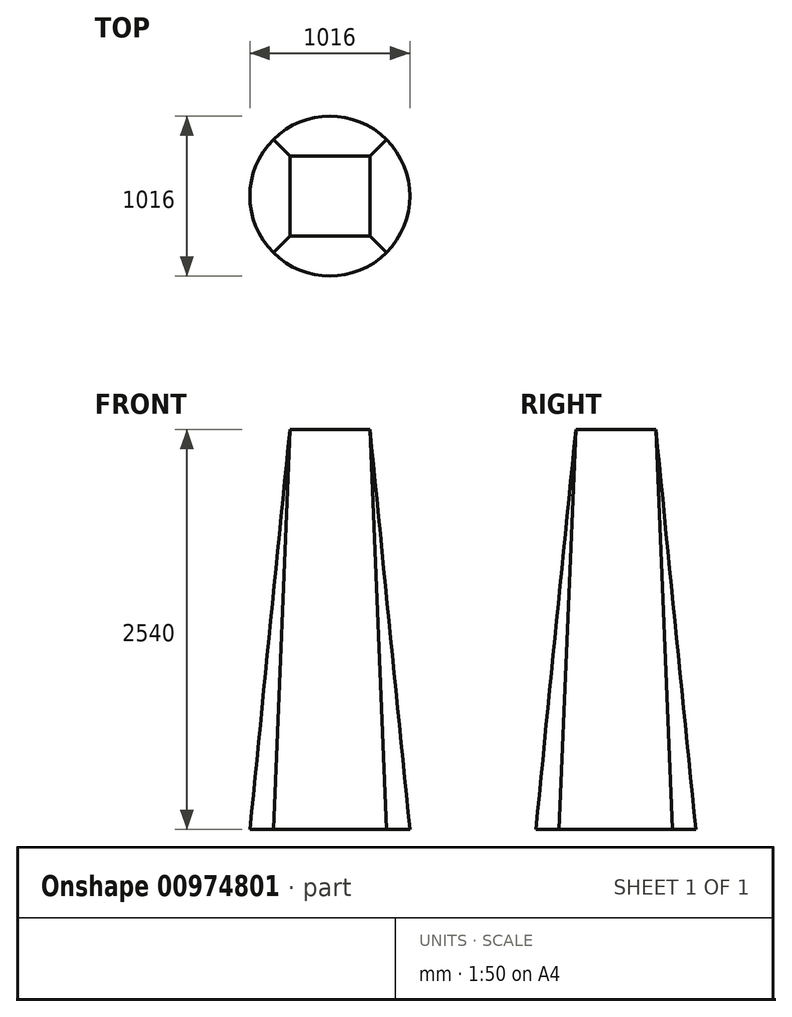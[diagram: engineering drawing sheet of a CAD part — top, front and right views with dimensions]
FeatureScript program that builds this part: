
annotation { "Feature Type Name" : "Feature", "Feature Type Description" : "" }
export const myFeature = defineFeature(function(context is Context, id is Id, definition is map)
    precondition{}
    {
        {
            var Q0;
            Q0=qCreatedBy(makeId("Top.planeOp"),FACE);
            var sketch = newSketch(context, id + "F0", { "sketchPlane" : qUnion([Q0])});
            skCircle(sketch, "E0", {"center": v(0, 0) * mm, "radius": 508 * mm});
            skSolve(sketch);
        }
        {
            var Q0;
            Q0=qCreatedBy(makeId("Top.planeOp"),FACE);
            cPlane(context, id + "F1", {"entities" : qUnion([Q0]), "cplaneType" : CPlaneType.OFFSET, "offset" : 2540 * mm, "width" : 152.4 * mm, "height" : 152.4 * mm});
        }
        {
            var Q0;
            Q0=qCreatedBy(id+"F1.planeOp",FACE);
            var sketch = newSketch(context, id + "F2", { "sketchPlane" : qUnion([Q0])});
            skLineSegment(sketch, "E1.bottom", {"start": v(254, 254) * mm, "end": v(-254, 254) * mm});
            skLineSegment(sketch, "E1.top", {"start": v(254, -254) * mm, "end": v(-254, -254) * mm});
            skLineSegment(sketch, "E1.left", {"start": v(254, 254) * mm, "end": v(254, -254) * mm});
            skLineSegment(sketch, "E1.right", {"start": v(-254, 254) * mm, "end": v(-254, -254) * mm});
            skPoint(sketch, "E1.middle", {"position": v(0, 0) * mm});
            skSolve(sketch);
        }
        {
            var Q0;
            Q0=makeQuery(id+"F0.imprint","IMPRINT",FACE,{"disambiguationData":[TD([[makeQuery(id+"F0.imprint","IMPRINT",EDGE,{"derivedFrom":sQuery(id+"F0.wireOp",EDGE,"E0")}),1.0]])]});
            var Q1;
            Q1=makeQuery(id+"F2.imprint","IMPRINT",FACE,{"disambiguationData":[TD([[makeQuery(id+"F2.imprint","IMPRINT",EDGE,{"derivedFrom":sQuery(id+"F2.wireOp",EDGE,"E1.bottom")}),1.0]])]});
            loft(context, id + "F3", {"sheetProfilesArray" : [{ "sheetProfileEntities" : qUnion([Q0]) }, { "sheetProfileEntities" : qUnion([Q1]) }]});
        }
    });
